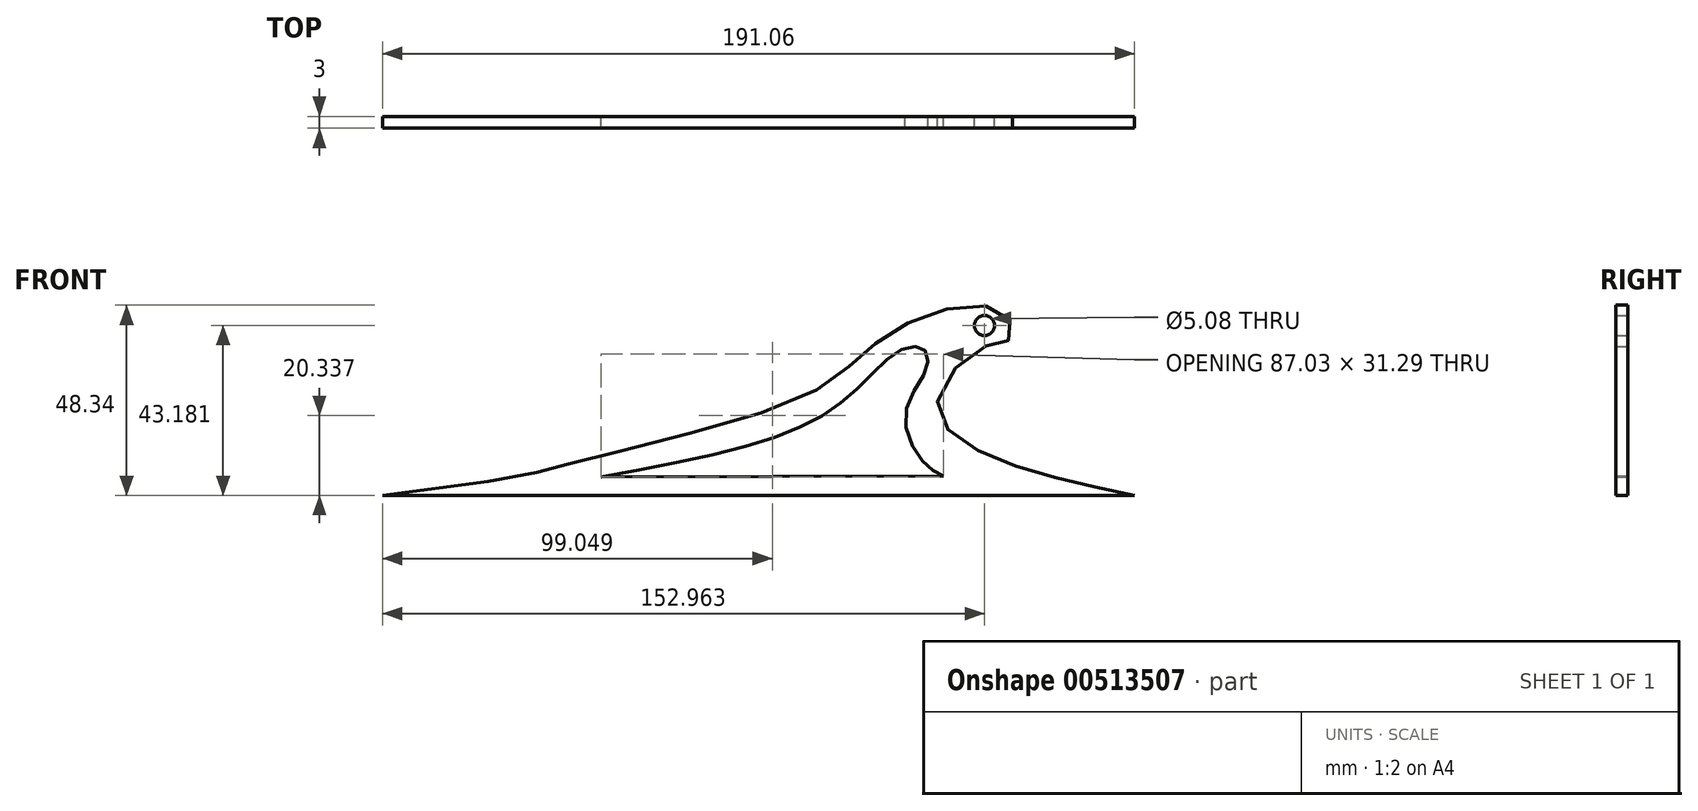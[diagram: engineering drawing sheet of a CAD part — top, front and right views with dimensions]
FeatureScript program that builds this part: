
annotation { "Feature Type Name" : "Feature", "Feature Type Description" : "" }
export const myFeature = defineFeature(function(context is Context, id is Id, definition is map)
    precondition{}
    {
        {
            var Q0;
            Q0=qCreatedBy(makeId("Front.planeOp"),FACE);
            var sketch = newSketch(context, id + "F0", { "sketchPlane" : qUnion([Q0])});
            skFitSpline(sketch, "E0", {"points": [v(-203.2, 0.2) * mm, v(-153.54, 8.82) * mm, v(-95.5, 25.7) * mm, v(-79.14, 37.84) * mm, v(-60.67, 47.33) * mm, v(-44.84, 46.28) * mm, v(-43.79, 39.95) * mm, v(-50.65, 37.84) * mm, v(-62.25, 23.6) * mm, v(-54.34, 13.04) * mm, v(-33.76, 5.12) * mm, v(-12.13, 0.2) * mm], "startDerivative": vector(862.98, 105.98) * mm, "endDerivative": vector(232.52, -48.04) * mm});
            skLineSegment(sketch, "E1", {"start": v(-203.2, 0.2) * mm, "end": v(-12.13, 0.2) * mm});
            skFitSpline(sketch, "E2", {"points": [v(-147.65, 4.88) * mm, v(-101.22, 15.8) * mm, v(-82.96, 26.96) * mm, v(-71.54, 37.1) * mm, v(-65.7, 37.36) * mm, v(-64.94, 32.54) * mm, v(-70.27, 21.12) * mm, v(-65.96, 8.82) * mm, v(-60.63, 5.14) * mm], "startDerivative": vector(223.67, 41.38) * mm, "endDerivative": vector(62.61, -29.92) * mm});
            skLineSegment(sketch, "E3", {"start": v(-147.65, 4.88) * mm, "end": v(-60.63, 5.14) * mm});
            skSolve(sketch);
        }
        {
            var Q0;
            Q0=makeQuery(id+"F0.imprint","IMPRINT",FACE,{"disambiguationData":[TD([[makeQuery(id+"F0.imprint","IMPRINT",EDGE,{"derivedFrom":sQuery(id+"F0.wireOp",EDGE,"E0")}),-1.0]])]});
            var Q1;
            Q1=makeQuery(id+"F0.imprint","IMPRINT",FACE,{"disambiguationData":[TD([[makeQuery(id+"F0.imprint","IMPRINT",EDGE,{"derivedFrom":sQuery(id+"F0.wireOp",EDGE,"90f449a7-4a10-47f7-98d8-1ac604535bbe0.MirrorCS")}),1.0]])]});
            extrude(context, id + "F1", {"entities" : qUnion([Q0, Q1]), "depth" : 3 * mm});
        }
        {
            var Q0;
            Q0=qCreatedBy(makeId("Front.planeOp"),FACE);
            var sketch = newSketch(context, id + "F2", { "sketchPlane" : qUnion([Q0])});
            skCircle(sketch, "E4", {"center": v(-50.23, 43.37) * mm, "radius": 2.54 * mm});
            skSolve(sketch);
        }
        {
            var Q0;
            Q0 = qSketchRegion(id + "F2", true);
            extrude(context, id + "F3", {"entities" : qUnion([Q0]), "operationType" : NewBodyOperationType.REMOVE, "depth" : 25.4 * mm, "offsetDistance" : 25.4 * mm});
        }
    });
